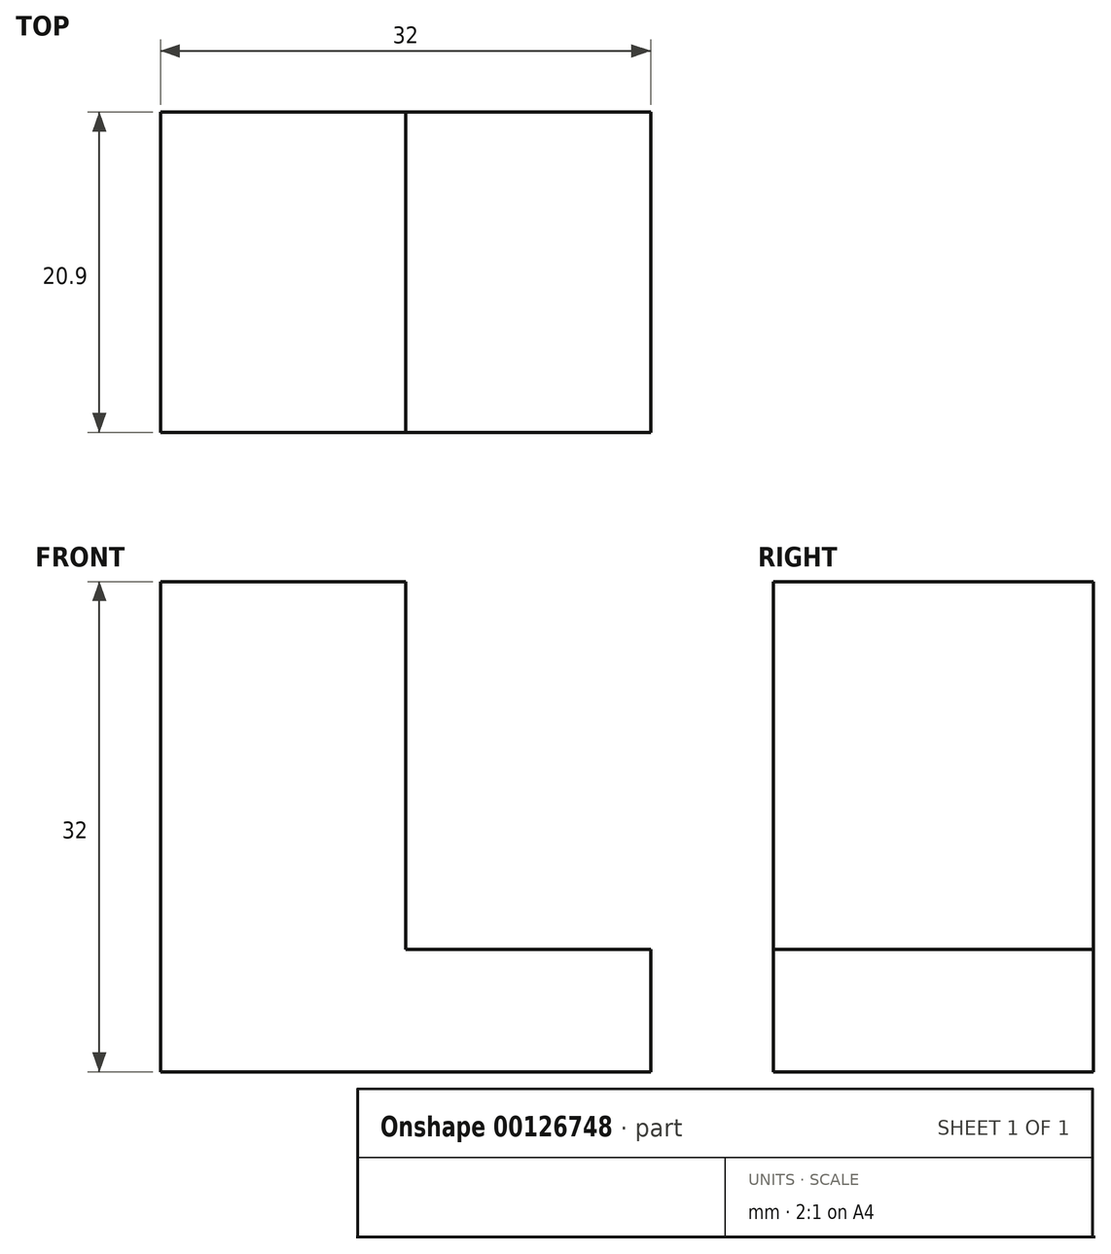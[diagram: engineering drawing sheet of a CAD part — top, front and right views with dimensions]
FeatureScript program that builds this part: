
annotation { "Feature Type Name" : "Feature", "Feature Type Description" : "" }
export const myFeature = defineFeature(function(context is Context, id is Id, definition is map)
    precondition{}
    {
        {
            var Q0;
            Q0=qCreatedBy(makeId("Front.planeOp"),FACE);
            var sketch = newSketch(context, id + "F0", { "sketchPlane" : qUnion([Q0])});
            skLineSegment(sketch, "E0", {"start": v(-32.72, 40.1) * mm, "end": v(-32.72, 16.1) * mm});
            skLineSegment(sketch, "E1", {"start": v(-32.72, 16.1) * mm, "end": v(-16.72, 16.1) * mm});
            skLineSegment(sketch, "E2", {"start": v(-16.72, 16.1) * mm, "end": v(-16.72, 8.1) * mm});
            skLineSegment(sketch, "E3", {"start": v(-48.72, 40.1) * mm, "end": v(-48.72, 8.1) * mm});
            skLineSegment(sketch, "E4", {"start": v(-32.72, 16.1) * mm, "end": v(-32.72, 8.1) * mm});
            skLineSegment(sketch, "E5", {"start": v(-32.72, 16.1) * mm, "end": v(-32.72, 24.1) * mm});
            skLineSegment(sketch, "E6", {"start": v(-32.72, 24.1) * mm, "end": v(-48.72, 24.1) * mm});
            skLineSegment(sketch, "E7", {"start": v(-40.72, 40.1) * mm, "end": v(-40.72, 24.1) * mm});
            skLineSegment(sketch, "E8", {"start": v(-24.72, 16.1) * mm, "end": v(-24.72, 8.1) * mm});
            skLineSegment(sketch, "E9", {"start": v(-16.72, 8.1) * mm, "end": v(-24.72, 8.1) * mm});
            skLineSegment(sketch, "E10", {"start": v(-24.72, 8.1) * mm, "end": v(-32.72, 8.1) * mm});
            skLineSegment(sketch, "E11", {"start": v(-32.72, 8.1) * mm, "end": v(-48.72, 8.1) * mm});
            skLineSegment(sketch, "E12", {"start": v(-32.72, 40.1) * mm, "end": v(-40.72, 40.1) * mm});
            skLineSegment(sketch, "E13", {"start": v(-48.72, 40.1) * mm, "end": v(-40.72, 40.1) * mm});
            skSolve(sketch);
        }
        {
            var Q0;
            {var subQ0=sQuery(id+"F0.wireOp",EDGE,"E2");Q0=makeQuery(id+"F0.imprint","IMPRINT",FACE,{"disambiguationData":[TD([[makeQuery(id+"F0.imprint","IMPRINT",EDGE,{"derivedFrom":subQ0}),-1.0]])]});}
            var Q1;
            {var subQ0=sQuery(id+"F0.wireOp",EDGE,"E4");Q1=makeQuery(id+"F0.imprint","IMPRINT",FACE,{"disambiguationData":[TD([[makeQuery(id+"F0.imprint","IMPRINT",EDGE,{"derivedFrom":subQ0}),1.0]])]});}
            var Q2;
            Q2=makeQuery(id+"F0.imprint","IMPRINT",FACE,{"disambiguationData":[TD([[makeQuery(id+"F0.imprint","IMPRINT",EDGE,{"derivedFrom":sQuery(id+"F0.wireOp",EDGE,"E4")}),-1.0]])]});
            var Q3;
            {var subQ0=sQuery(id+"F0.wireOp",EDGE,"E0");Q3=makeQuery(id+"F0.imprint","IMPRINT",FACE,{"disambiguationData":[TD([[makeQuery(id+"F0.imprint","IMPRINT",EDGE,{"derivedFrom":subQ0}),-1.0]])]});}
            var Q4;
            {var subQ4=sQuery(id+"F0.wireOp",EDGE,"E7");Q4=makeQuery(id+"F0.imprint","IMPRINT",FACE,{"disambiguationData":[TD([[makeQuery(id+"F0.imprint","IMPRINT",EDGE,{"derivedFrom":subQ4}),-1.0]])]});}
            extrude(context, id + "F1", {"entities" : qUnion([Q0, Q1, Q2, Q3, Q4]), "oppositeDirection" : true, "depth" : 20.9 * mm});
        }
    });
